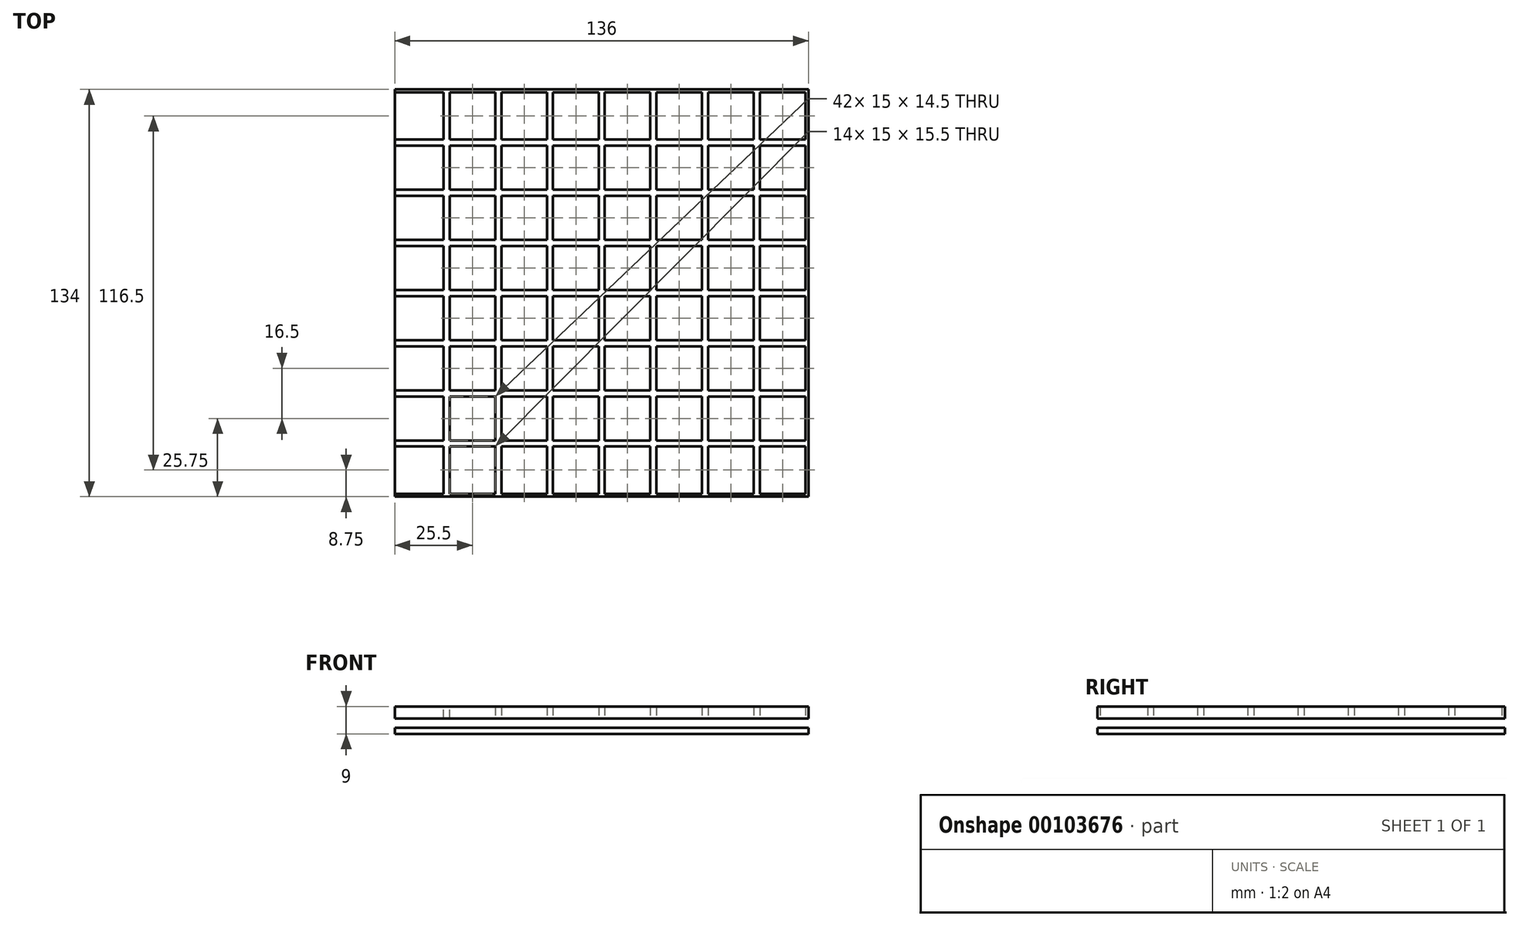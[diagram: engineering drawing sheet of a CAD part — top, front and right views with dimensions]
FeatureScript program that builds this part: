
annotation { "Feature Type Name" : "Feature", "Feature Type Description" : "" }
export const myFeature = defineFeature(function(context is Context, id is Id, definition is map)
    precondition{}
    {
        {
            var Q0;
            Q0=qCreatedBy(makeId("Front.planeOp"),FACE);
            var sketch = newSketch(context, id + "F0", { "sketchPlane" : qUnion([Q0])});
            skLineSegment(sketch, "E0.bottom", {"start": v(-68, 2) * mm, "end": v(68, 2) * mm});
            skLineSegment(sketch, "E0.top", {"start": v(-68, 0) * mm, "end": v(68, 0) * mm});
            skLineSegment(sketch, "E0.left", {"start": v(-68, 2) * mm, "end": v(-68, 0) * mm});
            skLineSegment(sketch, "E0.right", {"start": v(68, 2) * mm, "end": v(68, 0) * mm});
            skLineSegment(sketch, "E1.bottom", {"start": v(-68, 2) * mm, "end": v(-64.5, 2) * mm});
            skLineSegment(sketch, "E1.top", {"start": v(-68, 5) * mm, "end": v(-64.5, 5) * mm});
            skLineSegment(sketch, "E1.left", {"start": v(-68, 2) * mm, "end": v(-68, 5) * mm});
            skLineSegment(sketch, "E1.right", {"start": v(-64.5, 2) * mm, "end": v(-64.5, 5) * mm});
            skLineSegment(sketch, "E2.bottom", {"start": v(-20.5, 2) * mm, "end": v(-13.5, 2) * mm});
            skLineSegment(sketch, "E2.top", {"start": v(-20.5, 5) * mm, "end": v(-13.5, 5) * mm});
            skLineSegment(sketch, "E2.left", {"start": v(-20.5, 2) * mm, "end": v(-20.5, 5) * mm});
            skLineSegment(sketch, "E2.right", {"start": v(-13.5, 2) * mm, "end": v(-13.5, 5) * mm});
            skLineSegment(sketch, "E3.bottom", {"start": v(68, 2) * mm, "end": v(64.5, 2) * mm});
            skLineSegment(sketch, "E3.top", {"start": v(68, 5) * mm, "end": v(64.5, 5) * mm});
            skLineSegment(sketch, "E3.left", {"start": v(68, 2) * mm, "end": v(68, 5) * mm});
            skLineSegment(sketch, "E3.right", {"start": v(64.5, 2) * mm, "end": v(64.5, 5) * mm});
            skLineSegment(sketch, "E4.bottom", {"start": v(-54.5, 2) * mm, "end": v(-47.5, 2) * mm});
            skLineSegment(sketch, "E4.top", {"start": v(-54.5, 5) * mm, "end": v(-47.5, 5) * mm});
            skLineSegment(sketch, "E4.left", {"start": v(-54.5, 2) * mm, "end": v(-54.5, 5) * mm});
            skLineSegment(sketch, "E4.right", {"start": v(-47.5, 2) * mm, "end": v(-47.5, 5) * mm});
            skLineSegment(sketch, "E5.bottom", {"start": v(-37.5, 2) * mm, "end": v(-30.5, 2) * mm});
            skLineSegment(sketch, "E5.top", {"start": v(-37.5, 5) * mm, "end": v(-30.5, 5) * mm});
            skLineSegment(sketch, "E5.left", {"start": v(-37.5, 2) * mm, "end": v(-37.5, 5) * mm});
            skLineSegment(sketch, "E5.right", {"start": v(-30.5, 2) * mm, "end": v(-30.5, 5) * mm});
            skLineSegment(sketch, "E6.bottom", {"start": v(-3.5, 2) * mm, "end": v(3.5, 2) * mm});
            skLineSegment(sketch, "E6.top", {"start": v(-3.5, 5) * mm, "end": v(3.5, 5) * mm});
            skLineSegment(sketch, "E6.left", {"start": v(-3.5, 2) * mm, "end": v(-3.5, 5) * mm});
            skLineSegment(sketch, "E6.right", {"start": v(3.5, 2) * mm, "end": v(3.5, 5) * mm});
            skLineSegment(sketch, "E7.bottom", {"start": v(13.5, 2) * mm, "end": v(20.5, 2) * mm});
            skLineSegment(sketch, "E7.top", {"start": v(13.5, 5) * mm, "end": v(20.5, 5) * mm});
            skLineSegment(sketch, "E7.left", {"start": v(13.5, 2) * mm, "end": v(13.5, 5) * mm});
            skLineSegment(sketch, "E7.right", {"start": v(20.5, 2) * mm, "end": v(20.5, 5) * mm});
            skLineSegment(sketch, "E8.bottom", {"start": v(30.5, 2) * mm, "end": v(37.5, 2) * mm});
            skLineSegment(sketch, "E8.top", {"start": v(30.5, 5) * mm, "end": v(37.5, 5) * mm});
            skLineSegment(sketch, "E8.left", {"start": v(30.5, 2) * mm, "end": v(30.5, 5) * mm});
            skLineSegment(sketch, "E8.right", {"start": v(37.5, 2) * mm, "end": v(37.5, 5) * mm});
            skLineSegment(sketch, "E9.bottom", {"start": v(47.5, 2) * mm, "end": v(54.5, 2) * mm});
            skLineSegment(sketch, "E9.top", {"start": v(47.5, 5) * mm, "end": v(54.5, 5) * mm});
            skLineSegment(sketch, "E9.left", {"start": v(47.5, 2) * mm, "end": v(47.5, 5) * mm});
            skLineSegment(sketch, "E9.right", {"start": v(54.5, 2) * mm, "end": v(54.5, 5) * mm});
            skSolve(sketch);
        }
        {
            var Q0;
            Q0=makeQuery(id+"F0.imprint","IMPRINT",FACE,{"disambiguationData":[TD([[makeQuery(id+"F0.imprint","IMPRINT",EDGE,{"derivedFrom":sQuery(id+"F0.wireOp",EDGE,"E1.bottom")}),1.0]])]});
            var Q1;
            Q1=makeQuery(id+"F0.imprint","IMPRINT",FACE,{"disambiguationData":[TD([[makeQuery(id+"F0.imprint","IMPRINT",EDGE,{"derivedFrom":sQuery(id+"F0.wireOp",EDGE,"E2.bottom")}),1.0]])]});
            var Q2;
            Q2=makeQuery(id+"F0.imprint","IMPRINT",FACE,{"disambiguationData":[TD([[makeQuery(id+"F0.imprint","IMPRINT",EDGE,{"derivedFrom":sQuery(id+"F0.wireOp",EDGE,"E3.bottom")}),-1.0]])]});
            var Q3;
            Q3=makeQuery(id+"F0.imprint","IMPRINT",FACE,{"disambiguationData":[TD([[makeQuery(id+"F0.imprint","IMPRINT",EDGE,{"derivedFrom":sQuery(id+"F0.wireOp",EDGE,"E0.top")}),1.0]])]});
            var Q4;
            Q4=makeQuery(id+"F0.imprint","IMPRINT",FACE,{"disambiguationData":[TD([[makeQuery(id+"F0.imprint","IMPRINT",EDGE,{"derivedFrom":sQuery(id+"F0.wireOp",EDGE,"E4.bottom")}),1.0]])]});
            var Q5;
            Q5=makeQuery(id+"F0.imprint","IMPRINT",FACE,{"disambiguationData":[TD([[makeQuery(id+"F0.imprint","IMPRINT",EDGE,{"derivedFrom":sQuery(id+"F0.wireOp",EDGE,"E5.bottom")}),1.0]])]});
            var Q6;
            Q6=makeQuery(id+"F0.imprint","IMPRINT",FACE,{"disambiguationData":[TD([[makeQuery(id+"F0.imprint","IMPRINT",EDGE,{"derivedFrom":sQuery(id+"F0.wireOp",EDGE,"E6.bottom")}),1.0]])]});
            var Q7;
            Q7=makeQuery(id+"F0.imprint","IMPRINT",FACE,{"disambiguationData":[TD([[makeQuery(id+"F0.imprint","IMPRINT",EDGE,{"derivedFrom":sQuery(id+"F0.wireOp",EDGE,"E7.bottom")}),1.0]])]});
            var Q8;
            Q8=makeQuery(id+"F0.imprint","IMPRINT",FACE,{"disambiguationData":[TD([[makeQuery(id+"F0.imprint","IMPRINT",EDGE,{"derivedFrom":sQuery(id+"F0.wireOp",EDGE,"E8.bottom")}),1.0]])]});
            var Q9;
            Q9=makeQuery(id+"F0.imprint","IMPRINT",FACE,{"disambiguationData":[TD([[makeQuery(id+"F0.imprint","IMPRINT",EDGE,{"derivedFrom":sQuery(id+"F0.wireOp",EDGE,"E9.bottom")}),1.0]])]});
            extrude(context, id + "F1", {"entities" : qUnion([Q0, Q1, Q2, Q3, Q4, Q5, Q6, Q7, Q8, Q9]), "depth" : 134 * mm});
        }
        {
            var Q0;
            Q0=makeQuery(id+"F1.opExtrude","CAP_FACE",FACE,{"disambiguationData":[OSD([sQuery(id+"F0.wireOp",EDGE,"E0.bottom"),sQuery(id+"F0.wireOp",EDGE,"E0.top"),sQuery(id+"F0.wireOp",EDGE,"E0.left"),sQuery(id+"F0.wireOp",EDGE,"E0.right"),sQuery(id+"F0.wireOp",EDGE,"E1.top"),sQuery(id+"F0.wireOp",EDGE,"E1.left"),sQuery(id+"F0.wireOp",EDGE,"E1.right"),sQuery(id+"F0.wireOp",EDGE,"E2.top"),sQuery(id+"F0.wireOp",EDGE,"E2.left"),sQuery(id+"F0.wireOp",EDGE,"E2.right"),sQuery(id+"F0.wireOp",EDGE,"E3.top"),sQuery(id+"F0.wireOp",EDGE,"E3.left"),sQuery(id+"F0.wireOp",EDGE,"E3.right"),sQuery(id+"F0.wireOp",EDGE,"E4.top"),sQuery(id+"F0.wireOp",EDGE,"E4.left"),sQuery(id+"F0.wireOp",EDGE,"E4.right"),sQuery(id+"F0.wireOp",EDGE,"E5.top"),sQuery(id+"F0.wireOp",EDGE,"E5.left"),sQuery(id+"F0.wireOp",EDGE,"E5.right"),sQuery(id+"F0.wireOp",EDGE,"E6.top"),sQuery(id+"F0.wireOp",EDGE,"E6.left"),sQuery(id+"F0.wireOp",EDGE,"E6.right"),sQuery(id+"F0.wireOp",EDGE,"E7.top"),sQuery(id+"F0.wireOp",EDGE,"E7.left"),sQuery(id+"F0.wireOp",EDGE,"E7.right"),sQuery(id+"F0.wireOp",EDGE,"E8.top"),sQuery(id+"F0.wireOp",EDGE,"E8.left"),sQuery(id+"F0.wireOp",EDGE,"E8.right"),sQuery(id+"F0.wireOp",EDGE,"E9.top"),sQuery(id+"F0.wireOp",EDGE,"E9.left"),sQuery(id+"F0.wireOp",EDGE,"E9.right")])],"isStart":false});
            var sketch = newSketch(context, id + "F2", { "sketchPlane" : qUnion([Q0])});
            skLineSegment(sketch, "E10.bottom", {"start": v(-67, 5) * mm, "end": v(-68, 5) * mm});
            skLineSegment(sketch, "E10.top", {"start": v(-67, 9) * mm, "end": v(-68, 9) * mm});
            skLineSegment(sketch, "E10.left", {"start": v(-67, 5) * mm, "end": v(-67, 9) * mm});
            skLineSegment(sketch, "E10.right", {"start": v(-68, 5) * mm, "end": v(-68, 9) * mm});
            skLineSegment(sketch, "E11.bottom", {"start": v(-52, 5) * mm, "end": v(-50, 5) * mm});
            skLineSegment(sketch, "E11.top", {"start": v(-52, 9) * mm, "end": v(-50, 9) * mm});
            skLineSegment(sketch, "E11.left", {"start": v(-52, 5) * mm, "end": v(-52, 9) * mm});
            skLineSegment(sketch, "E11.right", {"start": v(-50, 5) * mm, "end": v(-50, 9) * mm});
            skLineSegment(sketch, "E12.1.0.0", {"start": v(-35, 5) * mm, "end": v(-35, 9) * mm});
            skLineSegment(sketch, "E12.1.0.1", {"start": v(-35, 9) * mm, "end": v(-33, 9) * mm});
            skLineSegment(sketch, "E12.1.0.2", {"start": v(-35, 5) * mm, "end": v(-33, 5) * mm});
            skLineSegment(sketch, "E12.1.0.3", {"start": v(-33, 5) * mm, "end": v(-33, 9) * mm});
            skLineSegment(sketch, "E12.2.0.0", {"start": v(-18, 5) * mm, "end": v(-18, 9) * mm});
            skLineSegment(sketch, "E12.2.0.1", {"start": v(-18, 9) * mm, "end": v(-16, 9) * mm});
            skLineSegment(sketch, "E12.2.0.2", {"start": v(-18, 5) * mm, "end": v(-16, 5) * mm});
            skLineSegment(sketch, "E12.2.0.3", {"start": v(-16, 5) * mm, "end": v(-16, 9) * mm});
            skLineSegment(sketch, "E12.3.0.0", {"start": v(-1, 5) * mm, "end": v(-1, 9) * mm});
            skLineSegment(sketch, "E12.3.0.1", {"start": v(-1, 9) * mm, "end": v(1, 9) * mm});
            skLineSegment(sketch, "E12.3.0.2", {"start": v(-1, 5) * mm, "end": v(1, 5) * mm});
            skLineSegment(sketch, "E12.3.0.3", {"start": v(1, 5) * mm, "end": v(1, 9) * mm});
            skLineSegment(sketch, "E12.4.0.0", {"start": v(16, 5) * mm, "end": v(16, 9) * mm});
            skLineSegment(sketch, "E12.4.0.1", {"start": v(16, 9) * mm, "end": v(18, 9) * mm});
            skLineSegment(sketch, "E12.4.0.2", {"start": v(16, 5) * mm, "end": v(18, 5) * mm});
            skLineSegment(sketch, "E12.4.0.3", {"start": v(18, 5) * mm, "end": v(18, 9) * mm});
            skLineSegment(sketch, "E12.5.0.0", {"start": v(33, 5) * mm, "end": v(33, 9) * mm});
            skLineSegment(sketch, "E12.5.0.1", {"start": v(33, 9) * mm, "end": v(35, 9) * mm});
            skLineSegment(sketch, "E12.5.0.2", {"start": v(33, 5) * mm, "end": v(35, 5) * mm});
            skLineSegment(sketch, "E12.5.0.3", {"start": v(35, 5) * mm, "end": v(35, 9) * mm});
            skLineSegment(sketch, "E12.direction1", {"start": v(-52, 5) * mm, "end": v(-35, 5) * mm, "construction": true});
            skPoint(sketch, "E13", {"position": v(-34, 5) * mm});
            skLineSegment(sketch, "E14.0.6.0", {"start": v(50, 5) * mm, "end": v(50, 9) * mm});
            skLineSegment(sketch, "E14.3.6.0", {"start": v(50, 9) * mm, "end": v(52, 9) * mm});
            skLineSegment(sketch, "E14.6.6.0", {"start": v(50, 5) * mm, "end": v(52, 5) * mm});
            skLineSegment(sketch, "E14.9.6.0", {"start": v(52, 5) * mm, "end": v(52, 9) * mm});
            skLineSegment(sketch, "E15.bottom", {"start": v(68, 5) * mm, "end": v(67, 5) * mm});
            skLineSegment(sketch, "E15.top", {"start": v(68, 9) * mm, "end": v(67, 9) * mm});
            skLineSegment(sketch, "E15.left", {"start": v(68, 5) * mm, "end": v(68, 9) * mm});
            skLineSegment(sketch, "E15.right", {"start": v(67, 5) * mm, "end": v(67, 9) * mm});
            skSolve(sketch);
        }
        {
            var Q0;
            Q0=makeQuery(id+"F2.imprint","IMPRINT",FACE,{"disambiguationData":[TD([[makeQuery(id+"F2.imprint","IMPRINT",EDGE,{"derivedFrom":sQuery(id+"F2.wireOp",EDGE,"E10.bottom")}),1.0]])]});
            var Q1;
            Q1=makeQuery(id+"F2.imprint","IMPRINT",FACE,{"disambiguationData":[TD([[makeQuery(id+"F2.imprint","IMPRINT",EDGE,{"derivedFrom":sQuery(id+"F2.wireOp",EDGE,"E11.bottom")}),1.0]])]});
            var Q2;
            Q2=makeQuery(id+"F2.imprint","IMPRINT",FACE,{"disambiguationData":[TD([[makeQuery(id+"F2.imprint","IMPRINT",EDGE,{"derivedFrom":sQuery(id+"F2.wireOp",EDGE,"E12.1.0.0")}),-1.0]])]});
            var Q3;
            Q3=makeQuery(id+"F2.imprint","IMPRINT",FACE,{"disambiguationData":[TD([[makeQuery(id+"F2.imprint","IMPRINT",EDGE,{"derivedFrom":sQuery(id+"F2.wireOp",EDGE,"E12.2.0.0")}),-1.0]])]});
            var Q4;
            Q4=makeQuery(id+"F2.imprint","IMPRINT",FACE,{"disambiguationData":[TD([[makeQuery(id+"F2.imprint","IMPRINT",EDGE,{"derivedFrom":sQuery(id+"F2.wireOp",EDGE,"E12.3.0.0")}),-1.0]])]});
            var Q5;
            Q5=makeQuery(id+"F2.imprint","IMPRINT",FACE,{"disambiguationData":[TD([[makeQuery(id+"F2.imprint","IMPRINT",EDGE,{"derivedFrom":sQuery(id+"F2.wireOp",EDGE,"E12.4.0.0")}),-1.0]])]});
            var Q6;
            Q6=makeQuery(id+"F2.imprint","IMPRINT",FACE,{"disambiguationData":[TD([[makeQuery(id+"F2.imprint","IMPRINT",EDGE,{"derivedFrom":sQuery(id+"F2.wireOp",EDGE,"E12.5.0.0")}),-1.0]])]});
            var Q7;
            Q7=makeQuery(id+"F2.imprint","IMPRINT",FACE,{"disambiguationData":[TD([[makeQuery(id+"F2.imprint","IMPRINT",EDGE,{"derivedFrom":sQuery(id+"F2.wireOp",EDGE,"E14.0.6.0")}),-1.0]])]});
            var Q8;
            Q8=makeQuery(id+"F2.imprint","IMPRINT",FACE,{"disambiguationData":[TD([[makeQuery(id+"F2.imprint","IMPRINT",EDGE,{"derivedFrom":sQuery(id+"F2.wireOp",EDGE,"E15.bottom")}),-1.0]])]});
            var Q9;
            Q9=makeQuery(id+"F1.opExtrude","CAP_FACE",FACE,{"disambiguationData":[OSD([sQuery(id+"F0.wireOp",EDGE,"E0.bottom"),sQuery(id+"F0.wireOp",EDGE,"E0.top"),sQuery(id+"F0.wireOp",EDGE,"E0.left"),sQuery(id+"F0.wireOp",EDGE,"E0.right"),sQuery(id+"F0.wireOp",EDGE,"E1.top"),sQuery(id+"F0.wireOp",EDGE,"E1.left"),sQuery(id+"F0.wireOp",EDGE,"E1.right"),sQuery(id+"F0.wireOp",EDGE,"E2.top"),sQuery(id+"F0.wireOp",EDGE,"E2.left"),sQuery(id+"F0.wireOp",EDGE,"E2.right"),sQuery(id+"F0.wireOp",EDGE,"E3.top"),sQuery(id+"F0.wireOp",EDGE,"E3.left"),sQuery(id+"F0.wireOp",EDGE,"E3.right"),sQuery(id+"F0.wireOp",EDGE,"E4.top"),sQuery(id+"F0.wireOp",EDGE,"E4.left"),sQuery(id+"F0.wireOp",EDGE,"E4.right"),sQuery(id+"F0.wireOp",EDGE,"E5.top"),sQuery(id+"F0.wireOp",EDGE,"E5.left"),sQuery(id+"F0.wireOp",EDGE,"E5.right"),sQuery(id+"F0.wireOp",EDGE,"E6.top"),sQuery(id+"F0.wireOp",EDGE,"E6.left"),sQuery(id+"F0.wireOp",EDGE,"E6.right"),sQuery(id+"F0.wireOp",EDGE,"E7.top"),sQuery(id+"F0.wireOp",EDGE,"E7.left"),sQuery(id+"F0.wireOp",EDGE,"E7.right"),sQuery(id+"F0.wireOp",EDGE,"E8.top"),sQuery(id+"F0.wireOp",EDGE,"E8.left"),sQuery(id+"F0.wireOp",EDGE,"E8.right"),sQuery(id+"F0.wireOp",EDGE,"E9.top"),sQuery(id+"F0.wireOp",EDGE,"E9.left"),sQuery(id+"F0.wireOp",EDGE,"E9.right")])],"isStart":true});
            extrude(context, id + "F3", {"entities" : qUnion([Q0, Q1, Q2, Q3, Q4, Q5, Q6, Q7, Q8]), "operationType" : NewBodyOperationType.ADD, "endBound" : BoundingType.UP_TO_SURFACE, "oppositeDirection" : true, "endBoundEntityFace" : qUnion([Q9]), "depth" : 25 * mm});
        }
        {
            var Q0;
            Q0=makeQuery(id+"F3.boolean.opBoolean","MERGE",FACE,{"derivedFrom":[makeQuery(id+"F1.opExtrude","SWEPT_FACE",FACE,{"disambiguationData":[OSD([sQuery(id+"F0.wireOp",EDGE,"E0.left"),sQuery(id+"F0.wireOp",EDGE,"E1.left")])]}),makeQuery(id+"F3.opExtrude","SWEPT_FACE",FACE,{"disambiguationData":[OSD([sQuery(id+"F2.wireOp",EDGE,"E10.right")])]})]});
            var sketch = newSketch(context, id + "F4", { "sketchPlane" : qUnion([Q0])});
            skLineSegment(sketch, "E16.bottom", {"start": v(0, 9) * mm, "end": v(1, 9) * mm});
            skLineSegment(sketch, "E16.top", {"start": v(0, 5) * mm, "end": v(1, 5) * mm});
            skLineSegment(sketch, "E16.left", {"start": v(0, 9) * mm, "end": v(0, 5) * mm});
            skLineSegment(sketch, "E16.right", {"start": v(1, 9) * mm, "end": v(1, 5) * mm});
            skLineSegment(sketch, "E17.bottom", {"start": v(16.5, 9) * mm, "end": v(18.5, 9) * mm});
            skLineSegment(sketch, "E17.top", {"start": v(16.5, 5) * mm, "end": v(18.5, 5) * mm});
            skLineSegment(sketch, "E17.left", {"start": v(16.5, 9) * mm, "end": v(16.5, 5) * mm});
            skLineSegment(sketch, "E17.right", {"start": v(18.5, 9) * mm, "end": v(18.5, 5) * mm});
            skLineSegment(sketch, "E18.1.0.0", {"start": v(35, 9) * mm, "end": v(35, 5) * mm});
            skLineSegment(sketch, "E18.1.0.1", {"start": v(33, 9) * mm, "end": v(33, 5) * mm});
            skLineSegment(sketch, "E18.1.0.2", {"start": v(33, 9) * mm, "end": v(35, 9) * mm});
            skLineSegment(sketch, "E18.1.0.3", {"start": v(33, 5) * mm, "end": v(35, 5) * mm});
            skLineSegment(sketch, "E18.2.0.0", {"start": v(51.5, 9) * mm, "end": v(51.5, 5) * mm});
            skLineSegment(sketch, "E18.2.0.1", {"start": v(49.5, 9) * mm, "end": v(49.5, 5) * mm});
            skLineSegment(sketch, "E18.2.0.2", {"start": v(49.5, 9) * mm, "end": v(51.5, 9) * mm});
            skLineSegment(sketch, "E18.2.0.3", {"start": v(49.5, 5) * mm, "end": v(51.5, 5) * mm});
            skLineSegment(sketch, "E18.3.0.0", {"start": v(68, 9) * mm, "end": v(68, 5) * mm});
            skLineSegment(sketch, "E18.3.0.1", {"start": v(66, 9) * mm, "end": v(66, 5) * mm});
            skLineSegment(sketch, "E18.3.0.2", {"start": v(66, 9) * mm, "end": v(68, 9) * mm});
            skLineSegment(sketch, "E18.3.0.3", {"start": v(66, 5) * mm, "end": v(68, 5) * mm});
            skLineSegment(sketch, "E18.4.0.0", {"start": v(84.5, 9) * mm, "end": v(84.5, 5) * mm});
            skLineSegment(sketch, "E18.4.0.1", {"start": v(82.5, 9) * mm, "end": v(82.5, 5) * mm});
            skLineSegment(sketch, "E18.4.0.2", {"start": v(82.5, 9) * mm, "end": v(84.5, 9) * mm});
            skLineSegment(sketch, "E18.4.0.3", {"start": v(82.5, 5) * mm, "end": v(84.5, 5) * mm});
            skLineSegment(sketch, "E18.5.0.0", {"start": v(101, 9) * mm, "end": v(101, 5) * mm});
            skLineSegment(sketch, "E18.5.0.1", {"start": v(99, 9) * mm, "end": v(99, 5) * mm});
            skLineSegment(sketch, "E18.5.0.2", {"start": v(99, 9) * mm, "end": v(101, 9) * mm});
            skLineSegment(sketch, "E18.5.0.3", {"start": v(99, 5) * mm, "end": v(101, 5) * mm});
            skLineSegment(sketch, "E18.6.0.0", {"start": v(117.5, 9) * mm, "end": v(117.5, 5) * mm});
            skLineSegment(sketch, "E18.6.0.1", {"start": v(115.5, 9) * mm, "end": v(115.5, 5) * mm});
            skLineSegment(sketch, "E18.6.0.2", {"start": v(115.5, 9) * mm, "end": v(117.5, 9) * mm});
            skLineSegment(sketch, "E18.6.0.3", {"start": v(115.5, 5) * mm, "end": v(117.5, 5) * mm});
            skLineSegment(sketch, "E18.direction1", {"start": v(18.5, 5) * mm, "end": v(35, 5) * mm, "construction": true});
            skLineSegment(sketch, "E19.bottom", {"start": v(133, 9) * mm, "end": v(134, 9) * mm});
            skLineSegment(sketch, "E19.top", {"start": v(133, 5) * mm, "end": v(134, 5) * mm});
            skLineSegment(sketch, "E19.left", {"start": v(133, 9) * mm, "end": v(133, 5) * mm});
            skLineSegment(sketch, "E19.right", {"start": v(134, 9) * mm, "end": v(134, 5) * mm});
            skSolve(sketch);
        }
        {
            var Q0;
            Q0 = qSketchRegion(id + "F4", true);
            var Q1;
            Q1=makeQuery(id+"F3.boolean.opBoolean","MERGE",FACE,{"derivedFrom":[makeQuery(id+"F1.opExtrude","SWEPT_FACE",FACE,{"disambiguationData":[OSD([sQuery(id+"F0.wireOp",EDGE,"E0.right"),sQuery(id+"F0.wireOp",EDGE,"E3.left")])]}),makeQuery(id+"F3.opExtrude","SWEPT_FACE",FACE,{"disambiguationData":[OSD([sQuery(id+"F2.wireOp",EDGE,"E15.left")])]})]});
            extrude(context, id + "F5", {"entities" : qUnion([Q0]), "operationType" : NewBodyOperationType.ADD, "endBound" : BoundingType.UP_TO_SURFACE, "oppositeDirection" : true, "endBoundEntityFace" : qUnion([Q1]), "depth" : 25 * mm});
        }
    });
